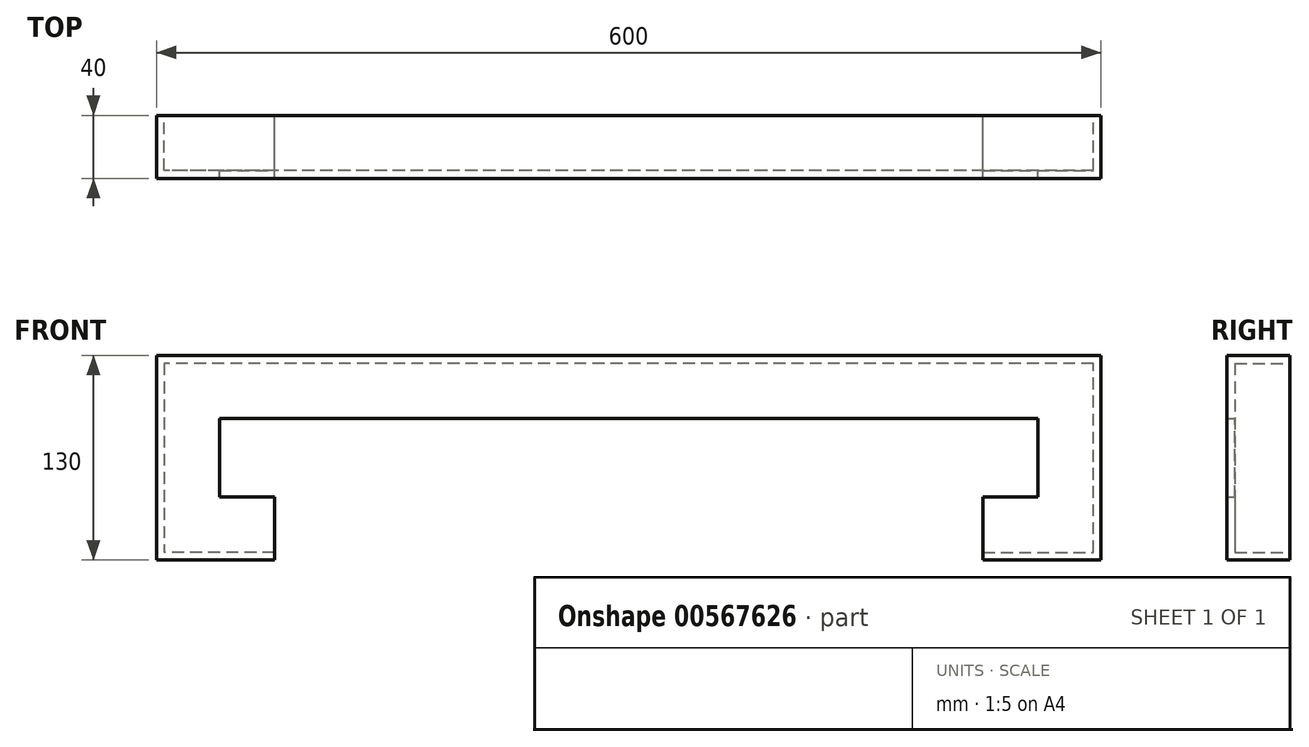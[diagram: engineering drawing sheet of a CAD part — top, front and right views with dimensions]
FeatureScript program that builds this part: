
annotation { "Feature Type Name" : "Feature", "Feature Type Description" : "" }
export const myFeature = defineFeature(function(context is Context, id is Id, definition is map)
    precondition{}
    {
        {
            var Q0;
            Q0=qCreatedBy(makeId("Top.planeOp"),FACE);
            var sketch = newSketch(context, id + "F0", { "sketchPlane" : qUnion([Q0])});
            skLineSegment(sketch, "E0.bottom", {"start": v(37.5, -20) * mm, "end": v(-37.5, -20) * mm});
            skLineSegment(sketch, "E0.top", {"start": v(37.5, 20) * mm, "end": v(-37.5, 20) * mm});
            skLineSegment(sketch, "E0.left", {"start": v(37.5, -20) * mm, "end": v(37.5, 20) * mm});
            skPoint(sketch, "E0.middle", {"position": v(0, 0) * mm});
            skLineSegment(sketch, "E1", {"start": v(0, -20) * mm, "end": v(-37.5, -20) * mm});
            skLineSegment(sketch, "E2", {"start": v(-37.5, 20) * mm, "end": v(-37.5, -20) * mm});
            skSolve(sketch);
        }
        {
            var Q0;
            Q0 = qSketchRegion(id + "F0", true);
            extrude(context, id + "F1", {"entities" : qUnion([Q0]), "oppositeDirection" : true, "depth" : 5 * mm, "offsetDistance" : 25 * mm});
        }
        {
            var Q0;
            Q0=makeQuery(id+"F1.opExtrude","CAP_FACE",FACE,{"disambiguationData":[OSD([sQuery(id+"F0.wireOp",EDGE,"E0.bottom"),sQuery(id+"F0.wireOp",EDGE,"E0.top"),sQuery(id+"F0.wireOp",EDGE,"E0.left"),sQuery(id+"F0.wireOp",EDGE,"E1"),sQuery(id+"F0.wireOp",EDGE,"E2")])],"isStart":true});
            var sketch = newSketch(context, id + "F2", { "sketchPlane" : qUnion([Q0])});
            skLineSegment(sketch, "E3", {"start": v(-37.5, 20) * mm, "end": v(-37.5, -20) * mm});
            skLineSegment(sketch, "E4", {"start": v(-37.5, -20) * mm, "end": v(2.5, -20) * mm});
            skLineSegment(sketch, "E5", {"start": v(2.5, -20) * mm, "end": v(2.5, -15) * mm});
            skLineSegment(sketch, "E6", {"start": v(2.5, -15) * mm, "end": v(-32.5, -15) * mm});
            skLineSegment(sketch, "E7", {"start": v(-32.5, -15) * mm, "end": v(-32.5, 20) * mm});
            skLineSegment(sketch, "E8", {"start": v(-32.5, 20) * mm, "end": v(-37.5, 20) * mm});
            skSolve(sketch);
        }
        {
            var Q0;
            Q0=makeQuery(id+"F2.imprint","IMPRINT",FACE,{"disambiguationData":[TD([[makeQuery(id+"F2.imprint","IMPRINT",EDGE,{"derivedFrom":sQuery(id+"F2.wireOp",EDGE,"E3")}),1.0]])]});
            extrude(context, id + "F3", {"entities" : qUnion([Q0]), "operationType" : NewBodyOperationType.ADD, "depth" : 120 * mm, "offsetDistance" : 25 * mm});
        }
        {
            var Q0;
            Q0=makeQuery(id+"F3.opExtrude","CAP_FACE",FACE,{"disambiguationData":[OSD([sQuery(id+"F2.wireOp",EDGE,"E3"),sQuery(id+"F2.wireOp",EDGE,"E4"),sQuery(id+"F2.wireOp",EDGE,"E5"),sQuery(id+"F2.wireOp",EDGE,"E6"),sQuery(id+"F2.wireOp",EDGE,"E7"),sQuery(id+"F2.wireOp",EDGE,"E8")])],"isStart":false});
            var sketch = newSketch(context, id + "F4", { "sketchPlane" : qUnion([Q0])});
            skLineSegment(sketch, "E9.bottom", {"start": v(-37.5, 20) * mm, "end": v(562.5, 20) * mm});
            skLineSegment(sketch, "E9.top", {"start": v(-37.5, -20) * mm, "end": v(562.5, -20) * mm});
            skLineSegment(sketch, "E9.left", {"start": v(-37.5, 20) * mm, "end": v(-37.5, -20) * mm});
            skLineSegment(sketch, "E9.right", {"start": v(562.5, 20) * mm, "end": v(562.5, -20) * mm});
            skSolve(sketch);
        }
        {
            var Q0;
            Q0 = qSketchRegion(id + "F4", true);
            extrude(context, id + "F5", {"entities" : qUnion([Q0]), "operationType" : NewBodyOperationType.ADD, "depth" : 5 * mm, "offsetDistance" : 25 * mm});
        }
        {
            var Q0;
            Q0=makeQuery(id+"F5.opExtrude","CAP_FACE",FACE,{"disambiguationData":[OSD([sQuery(id+"F4.wireOp",EDGE,"E9.bottom"),sQuery(id+"F4.wireOp",EDGE,"E9.top"),sQuery(id+"F4.wireOp",EDGE,"E9.left"),sQuery(id+"F4.wireOp",EDGE,"E9.right")])],"isStart":true});
            var sketch = newSketch(context, id + "F6", { "sketchPlane" : qUnion([Q0])});
            skLineSegment(sketch, "E10", {"start": v(562.5, -20) * mm, "end": v(562.5, 20) * mm});
            skLineSegment(sketch, "E11", {"start": v(562.5, 20) * mm, "end": v(522.5, 20) * mm});
            skLineSegment(sketch, "E12", {"start": v(522.5, 20) * mm, "end": v(522.5, 15) * mm});
            skLineSegment(sketch, "E13", {"start": v(522.5, 15) * mm, "end": v(557.5, 15) * mm});
            skLineSegment(sketch, "E14", {"start": v(557.5, 15) * mm, "end": v(557.5, -20) * mm});
            skLineSegment(sketch, "E15", {"start": v(557.5, -20) * mm, "end": v(562.5, -20) * mm});
            skSolve(sketch);
        }
        {
            var Q0;
            Q0 = qSketchRegion(id + "F6", true);
            extrude(context, id + "F7", {"entities" : qUnion([Q0]), "operationType" : NewBodyOperationType.ADD, "depth" : 120 * mm, "offsetDistance" : 25 * mm});
        }
        {
            var Q0;
            Q0=makeQuery(id+"F7.opExtrude","CAP_FACE",FACE,{"disambiguationData":[OSD([sQuery(id+"F6.wireOp",EDGE,"E10"),sQuery(id+"F6.wireOp",EDGE,"E11"),sQuery(id+"F6.wireOp",EDGE,"E12"),sQuery(id+"F6.wireOp",EDGE,"E13"),sQuery(id+"F6.wireOp",EDGE,"E14"),sQuery(id+"F6.wireOp",EDGE,"E15")])],"isStart":false});
            var sketch = newSketch(context, id + "F8", { "sketchPlane" : qUnion([Q0])});
            skLineSegment(sketch, "E16.right", {"start": v(562.5, 20) * mm, "end": v(562.5, -20) * mm});
            skLineSegment(sketch, "E17.bottom", {"start": v(562.5, 20) * mm, "end": v(487.5, 20) * mm});
            skLineSegment(sketch, "E17.top", {"start": v(562.5, -20) * mm, "end": v(487.5, -20) * mm});
            skLineSegment(sketch, "E17.right", {"start": v(487.5, 20) * mm, "end": v(487.5, -20) * mm});
            skSolve(sketch);
        }
        {
            var Q0;
            Q0 = qSketchRegion(id + "F8", true);
            extrude(context, id + "F9", {"entities" : qUnion([Q0]), "operationType" : NewBodyOperationType.ADD, "depth" : 5 * mm, "offsetDistance" : 25 * mm});
        }
        {
            var Q0;
            Q0=makeQuery(id+"F3.opExtrude","SWEPT_FACE",FACE,{"disambiguationData":[OSD([sQuery(id+"F2.wireOp",EDGE,"E5")])]});
            var sketch = newSketch(context, id + "F10", { "sketchPlane" : qUnion([Q0])});
            skLineSegment(sketch, "E18", {"start": v(-20, 120) * mm, "end": v(-20, 85) * mm});
            skLineSegment(sketch, "E19", {"start": v(-20, 85) * mm, "end": v(-15, 85) * mm});
            skLineSegment(sketch, "E20", {"start": v(-15, 85) * mm, "end": v(-15, 120) * mm});
            skSolve(sketch);
        }
        {
            var Q0;
            Q0 = qSketchRegion(id + "F10", true);
            var Q1;
            Q1=makeQuery(id+"F10.imprint","IMPRINT",FACE,{"disambiguationData":[TD([[makeQuery(id+"F10.imprint","IMPRINT",EDGE,{"derivedFrom":sQuery(id+"F10.wireOp",EDGE,"E18")}),1.0]])]});
            extrude(context, id + "F11", {"entities" : qUnion([Q0, Q1]), "operationType" : NewBodyOperationType.ADD, "depth" : 520 * mm, "offsetDistance" : 25 * mm});
        }
        {
            var Q0;
            Q0=makeQuery(id+"F1.opExtrude","CAP_FACE",FACE,{"disambiguationData":[OSD([sQuery(id+"F0.wireOp",EDGE,"E0.bottom"),sQuery(id+"F0.wireOp",EDGE,"E0.top"),sQuery(id+"F0.wireOp",EDGE,"E0.left"),sQuery(id+"F0.wireOp",EDGE,"E1"),sQuery(id+"F0.wireOp",EDGE,"E2")])],"isStart":true});
            var sketch = newSketch(context, id + "F12", { "sketchPlane" : qUnion([Q0])});
            skLineSegment(sketch, "E21", {"start": v(2.5, -15) * mm, "end": v(37.5, -15) * mm});
            skSolve(sketch);
        }
        {
            var Q0;
            Q0 = qSketchRegion(id + "F12", true);
            var Q1;
            {var subQ0=sQuery(id+"F12.wireOp",EDGE,"E21");Q1=makeQuery(id+"F12.imprint","IMPRINT",FACE,{"disambiguationData":[TD([[makeQuery(id+"F12.imprint","IMPRINT",EDGE,{"derivedFrom":subQ0}),-1.0]])]});}
            extrude(context, id + "F13", {"entities" : qUnion([Q0, Q1]), "operationType" : NewBodyOperationType.ADD, "depth" : 35 * mm, "offsetDistance" : 25 * mm});
        }
        {
            var Q0;
            Q0=makeQuery(id+"F9.opExtrude","CAP_FACE",FACE,{"disambiguationData":[OSD([sQuery(id+"F8.wireOp",EDGE,"E17.bottom"),sQuery(id+"F8.wireOp",EDGE,"E17.top"),sQuery(id+"F8.wireOp",EDGE,"E16.right"),sQuery(id+"F8.wireOp",EDGE,"E17.right")])],"isStart":true});
            var sketch = newSketch(context, id + "F14", { "sketchPlane" : qUnion([Q0])});
            skLineSegment(sketch, "E22", {"start": v(522.5, -15) * mm, "end": v(487.5, -15) * mm});
            skSolve(sketch);
        }
        {
            var Q0;
            Q0 = qSketchRegion(id + "F14", true);
            var Q1;
            {var subQ0=sQuery(id+"F14.wireOp",EDGE,"E22");Q1=makeQuery(id+"F14.imprint","IMPRINT",FACE,{"disambiguationData":[TD([[makeQuery(id+"F14.imprint","IMPRINT",EDGE,{"derivedFrom":subQ0}),1.0]])]});}
            extrude(context, id + "F15", {"entities" : qUnion([Q0, Q1]), "operationType" : NewBodyOperationType.ADD, "depth" : 35 * mm, "offsetDistance" : 25 * mm});
        }
    });
